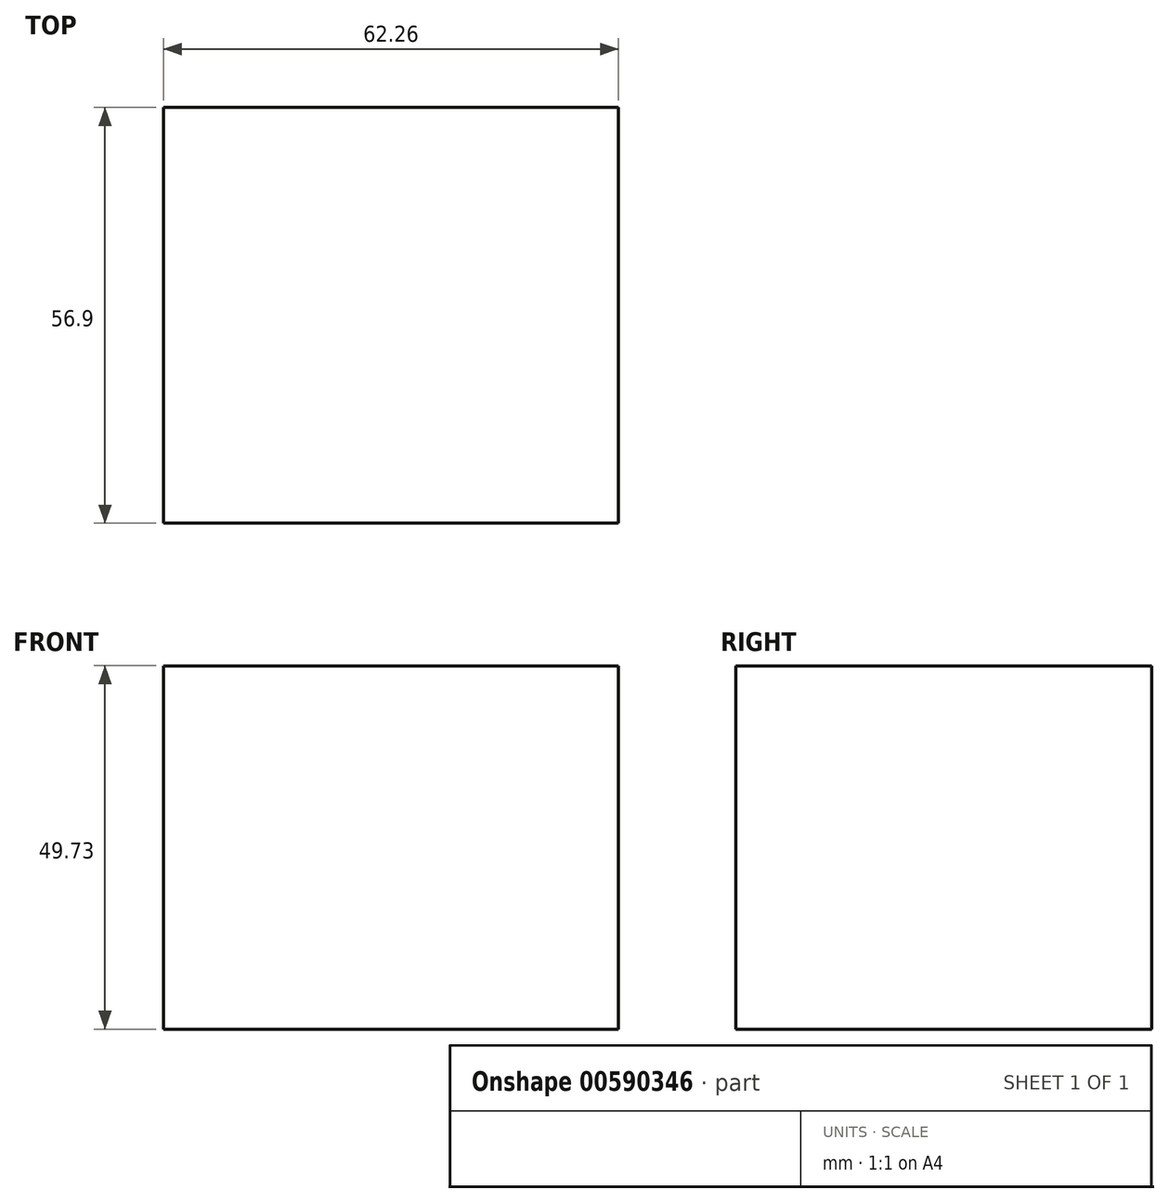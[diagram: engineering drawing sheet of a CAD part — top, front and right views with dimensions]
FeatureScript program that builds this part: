
annotation { "Feature Type Name" : "Feature", "Feature Type Description" : "" }
export const myFeature = defineFeature(function(context is Context, id is Id, definition is map)
    precondition{}
    {
        {
            var Q0;
            Q0=qCreatedBy(makeId("Front.planeOp"),FACE);
            var sketch = newSketch(context, id + "F0", { "sketchPlane" : qUnion([Q0])});
            skLineSegment(sketch, "E0.bottom", {"start": v(25.22, -3.87) * mm, "end": v(-37.04, -3.87) * mm});
            skLineSegment(sketch, "E0.top", {"start": v(25.22, 45.86) * mm, "end": v(-37.04, 45.86) * mm});
            skLineSegment(sketch, "E0.left", {"start": v(25.22, -3.87) * mm, "end": v(25.22, 45.86) * mm});
            skLineSegment(sketch, "E0.right", {"start": v(-37.04, -3.87) * mm, "end": v(-37.04, 45.86) * mm});
            skSolve(sketch);
        }
        {
            var Q0;
            Q0=makeQuery(id+"F0.imprint","IMPRINT",FACE,{"disambiguationData":[TD([[makeQuery(id+"F0.imprint","IMPRINT",EDGE,{"derivedFrom":sQuery(id+"F0.wireOp",EDGE,"E0.bottom")}),-1.0]])]});
            extrude(context, id + "F1", {"entities" : qUnion([Q0]), "depth" : 56.9 * mm, "offsetDistance" : 25.4 * mm});
        }
        {
            var Q0;
            Q0=makeQuery(id+"F1.opExtrude","SWEPT_FACE",FACE,{"disambiguationData":[OSD([sQuery(id+"F0.wireOp",EDGE,"E0.top")])]});
            extrude(context, id + "F2", {"entities" : qUnion([Q0]), "operationType" : NewBodyOperationType.ADD, "oppositeDirection" : true, "depth" : 11.43 * mm, "offsetDistance" : 25.4 * mm});
        }
    });
